# Revit family: QF_Summit_HC30WW_Under Cabinet Convertible Range Hood
name_source: partatom
category: Specialty Equipment
units: mm (PartAtom-declared; Revit-internal decimal feet)

## family parameters
Always vertical = Yes
Cut with Voids When Loaded = No
Part Type = Normal
Room Calculation Point = No
Round Connector Dimension = Use Diameter
Shared = No
Work Plane-Based = No

## types (1)
- QF_Summit_HC30WW_Under Cabinet Convertible Range Hood
    Apparent Power = 196 VA
    Conn Conduit = Yes
    Cycle = 60 Hz
    Default Elevation = 0"
    Depth = 20"
    Description = Under Cabinet Convertible Range Hood
    Elec Conn Connection Height = 0"
    Elec Conn RI Height = 0"
    Exhaust RI Height = 0"
    Exhaust Static Press = 0.00 in-wg
    Exhaust Vent Depth = 0"
    Exhaust Vent Diameter = 0"
    Exhaust Vent Width = 0"
    Exhaust Volume = 0 CFM
    FL Amps = 2 A
    Foodservice Equipment Identifier = Yes
    Height = 5 1/2"
    Identify Quantity as Lot = Yes
    Length = 29 7/8"
    MU Air RI Height = 0"
    MU Air Static Press = 0.00 in-wg
    MU Air Vent Depth = 0"
    MU Air Vent Diameter = 0"
    MU Air Vent Width = 0"
    MU Air Volume = 300 CFM
    Manufacturer = Summit
    Max Overcurrent Protection = 0 A
    Min Ckt Ampacity = 0 A
    Model = HC30WW
    Number of Poles = 1
    Phase = 1
    Ventilation Remarks = 3.25 inches x 10 inches rectangular or 0.86 inches round with transition with transition
    Volts = 115 V
    Watts = 196 W
    Weight in Pounds = 13

## geometry (parser evidence)
native form markers: Sweep x2
no freeform markers — native parametric forms only
